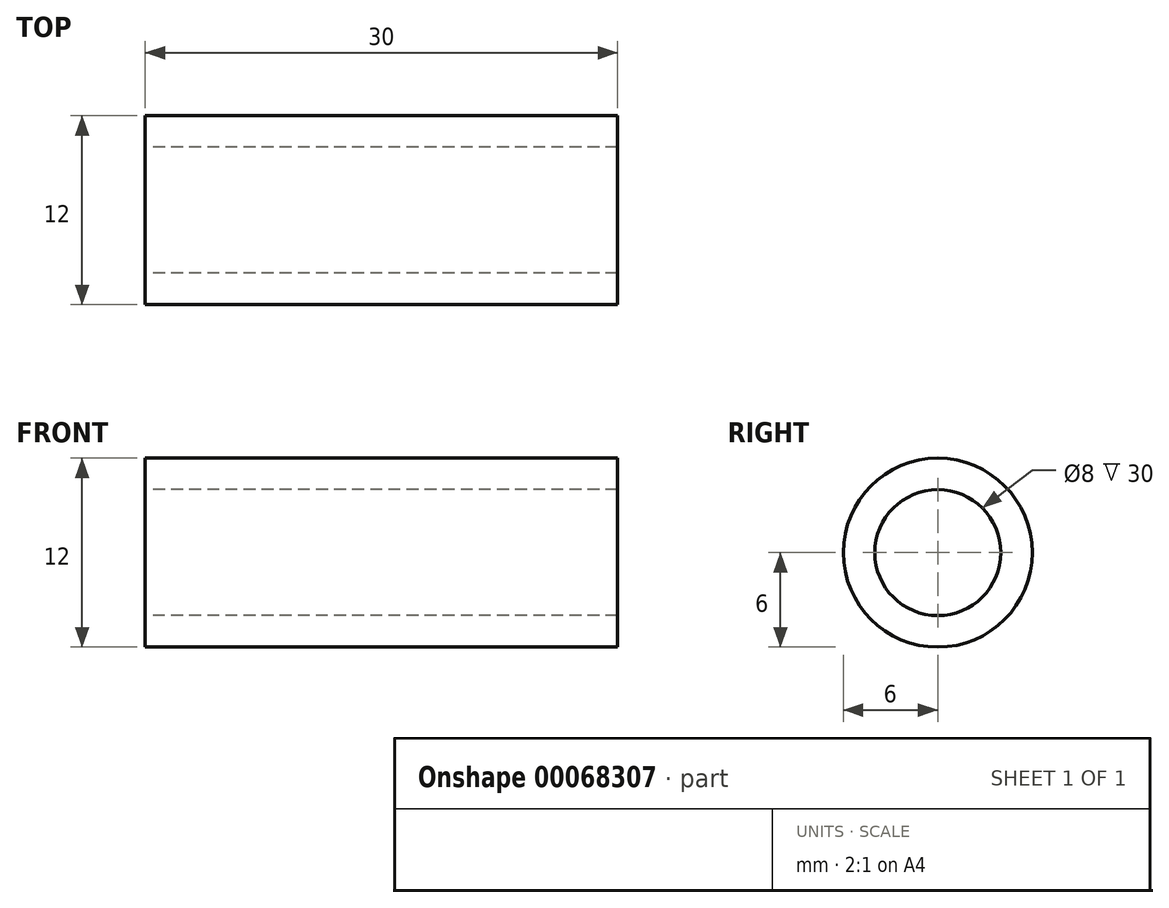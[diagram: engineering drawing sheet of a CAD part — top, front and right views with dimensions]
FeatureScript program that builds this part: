
annotation { "Feature Type Name" : "Feature", "Feature Type Description" : "" }
export const myFeature = defineFeature(function(context is Context, id is Id, definition is map)
    precondition{}
    {
        {
            var Q0;
            Q0=qCreatedBy(makeId("Right.planeOp"),FACE);
            var sketch = newSketch(context, id + "F0", { "sketchPlane" : qUnion([Q0])});
            skCircle(sketch, "E0", {"center": v(0, 0) * mm, "radius": 4 * mm});
            skCircle(sketch, "E1", {"center": v(0, 0) * mm, "radius": 6 * mm});
            skSolve(sketch);
        }
        {
            var Q0;
            Q0 = qSketchRegion(id + "F0", true);
            extrude(context, id + "F1", {"entities" : qUnion([Q0]), "depth" : 30 * mm});
        }
    });
